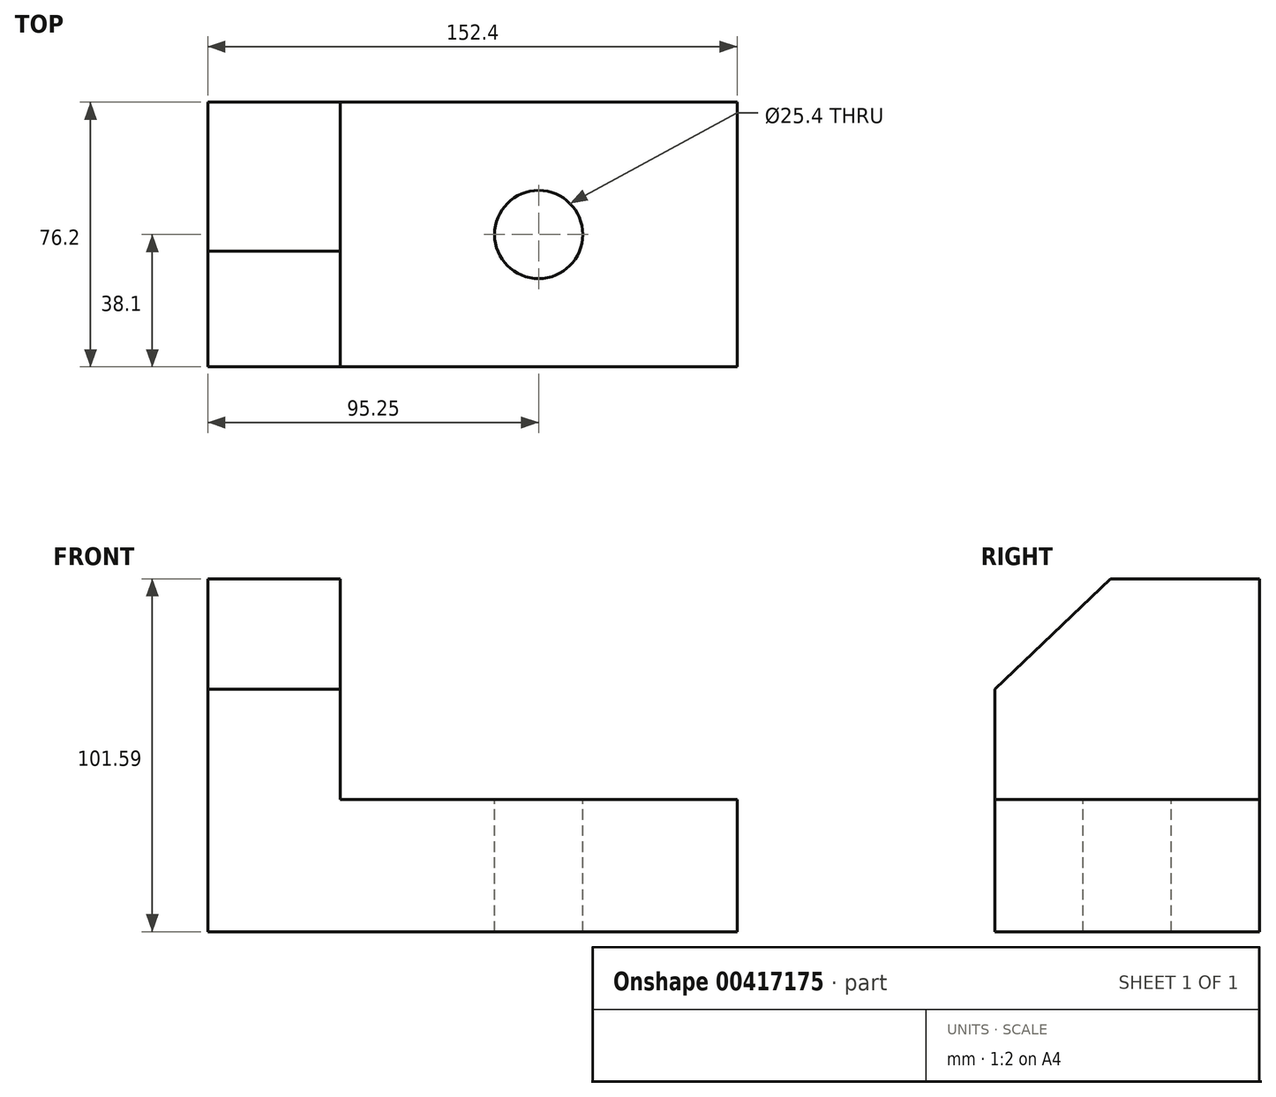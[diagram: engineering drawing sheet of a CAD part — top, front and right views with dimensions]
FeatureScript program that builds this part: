
annotation { "Feature Type Name" : "Feature", "Feature Type Description" : "" }
export const myFeature = defineFeature(function(context is Context, id is Id, definition is map)
    precondition{}
    {
        {
            var Q0;
            Q0=qCreatedBy(makeId("Front.planeOp"),FACE);
            var sketch = newSketch(context, id + "F0", { "sketchPlane" : qUnion([Q0])});
            skLineSegment(sketch, "E0", {"start": v(0, 0) * mm, "end": v(152.4, 0) * mm});
            skLineSegment(sketch, "E1", {"start": v(152.4, 0) * mm, "end": v(152.4, 38.1) * mm});
            skLineSegment(sketch, "E2", {"start": v(152.4, 38.1) * mm, "end": v(38.1, 38.1) * mm});
            skLineSegment(sketch, "E3", {"start": v(38.1, 38.1) * mm, "end": v(38.1, 101.59) * mm});
            skLineSegment(sketch, "E4", {"start": v(38.1, 101.59) * mm, "end": v(0, 101.59) * mm});
            skLineSegment(sketch, "E5", {"start": v(0, 101.59) * mm, "end": v(0, -0.01) * mm});
            skSolve(sketch);
        }
        {
            var Q0;
            {var subQ0=sQuery(id+"F0.wireOp",EDGE,"E0");Q0=makeQuery(id+"F0.imprint","IMPRINT",FACE,{"disambiguationData":[TD([[makeQuery(id+"F0.imprint","IMPRINT",EDGE,{"derivedFrom":subQ0}),1.0]])]});}
            extrude(context, id + "F1", {"entities" : qUnion([Q0]), "depth" : 76.2 * mm});
        }
        {
            var Q0;
            Q0=makeQuery(id+"F1.opExtrude","SWEPT_FACE",FACE,{"disambiguationData":[OSD([sQuery(id+"F0.wireOp",EDGE,"E3")])]});
            var sketch = newSketch(context, id + "F2", { "sketchPlane" : qUnion([Q0])});
            skLineSegment(sketch, "E6", {"start": v(-42.88, 101.59) * mm, "end": v(-76.2, 69.84) * mm});
            skSolve(sketch);
        }
        {
            var Q0;
            {var subQ0=sQuery(id+"F2.wireOp",EDGE,"E6");Q0=makeQuery(id+"F2.imprint","IMPRINT",FACE,{"disambiguationData":[TD([[makeQuery(id+"F2.imprint","IMPRINT",EDGE,{"derivedFrom":subQ0}),-1.0]])]});}
            extrude(context, id + "F3", {"entities" : qUnion([Q0]), "operationType" : NewBodyOperationType.REMOVE, "endBound" : BoundingType.THROUGH_ALL, "oppositeDirection" : true, "depth" : 25.4 * mm});
        }
        {
            var Q0;
            Q0=makeQuery(id+"F1.opExtrude","SWEPT_FACE",FACE,{"disambiguationData":[OSD([sQuery(id+"F0.wireOp",EDGE,"E2")])]});
            var sketch = newSketch(context, id + "F4", { "sketchPlane" : qUnion([Q0])});
            skLineSegment(sketch, "E7", {"start": v(38.1, -76.2) * mm, "end": v(152.4, 0) * mm, "construction": true});
            skCircle(sketch, "E8", {"center": v(95.25, -38.1) * mm, "radius": 12.7 * mm});
            skSolve(sketch);
        }
        {
            var Q0;
            Q0=makeQuery(id+"F4.imprint","IMPRINT",FACE,{"disambiguationData":[TD([[makeQuery(id+"F4.imprint","IMPRINT",EDGE,{"derivedFrom":sQuery(id+"F4.wireOp",EDGE,"E8")}),1.0]])]});
            extrude(context, id + "F5", {"entities" : qUnion([Q0]), "operationType" : NewBodyOperationType.REMOVE, "endBound" : BoundingType.THROUGH_ALL, "oppositeDirection" : true, "depth" : 25.4 * mm});
        }
    });
